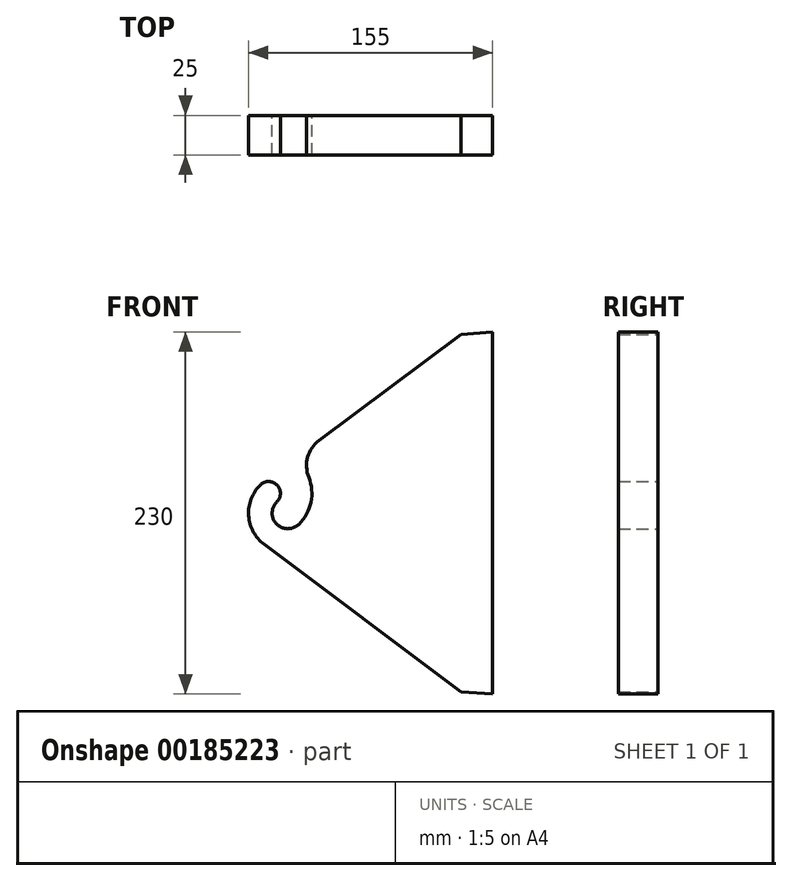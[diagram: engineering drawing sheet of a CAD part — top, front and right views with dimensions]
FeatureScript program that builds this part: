
annotation { "Feature Type Name" : "Feature", "Feature Type Description" : "" }
export const myFeature = defineFeature(function(context is Context, id is Id, definition is map)
    precondition{}
    {
        {
            var Q0;
            Q0=qCreatedBy(makeId("Front.planeOp"),FACE);
            var sketch = newSketch(context, id + "F0", { "sketchPlane" : qUnion([Q0])});
            skCircle(sketch, "E0", {"center": v(-130, 130) * mm, "radius": 105 * mm, "construction": true});
            skCircle(sketch, "E1", {"center": v(-130, 130) * mm, "radius": 26.5 * mm, "construction": true});
            skArc(sketch, "E2", {"start": v(-137, 137.14) * mm, "mid": v(-137.14, 123) * mm, "end": v(-123, 122.86) * mm});
            skLineSegment(sketch, "E3", {"start": v(-130, 130) * mm, "end": v(0, 130) * mm, "construction": true});
            skLineSegment(sketch, "E4", {"start": v(0, 245) * mm, "end": v(0, 15) * mm});
            skArc(sketch, "E5", {"start": v(-147.5, 147.86) * mm, "mid": v(-154.94, 128.34) * mm, "end": v(-144.97, 109.98) * mm});
            skLineSegment(sketch, "E6", {"start": v(0, 245) * mm, "end": v(-19.94, 243.51) * mm});
            skLineSegment(sketch, "E7", {"start": v(-19.94, 243.51) * mm, "end": v(-110.1, 176.1) * mm});
            skLineSegment(sketch, "E8.MirrorCS", {"start": v(-19.94, 16.49) * mm, "end": v(-144.97, 109.98) * mm});
            skLineSegment(sketch, "E9.MirrorCS", {"start": v(0, 15) * mm, "end": v(-19.94, 16.49) * mm});
            skArc(sketch, "E10", {"start": v(-137, 137.14) * mm, "mid": v(-136.9, 147.75) * mm, "end": v(-147.5, 147.86) * mm});
            skArc(sketch, "E11", {"start": v(-153.26, 117.3) * mm, "mid": v(-152.14, 116.84) * mm, "end": v(-151, 116.43) * mm});
            skPoint(sketch, "E12.orphan", {"position": v(-144.97, 150.02) * mm});
            skArc(sketch, "E13.trimOffspring", {"start": v(-123, 122.86) * mm, "mid": v(-115.34, 136.81) * mm, "end": v(-116.7, 152.68) * mm});
            skPoint(sketch, "E14.visualSharp", {"position": v(-125.68, 164.45) * mm});
            skArc(sketch, "E14.filletArc", {"start": v(-110.1, 176.1) * mm, "mid": v(-117.37, 165.5) * mm, "end": v(-116.7, 152.68) * mm});
            skSolve(sketch);
        }
        {
            var Q0;
            Q0=makeQuery(id+"F0.imprint","IMPRINT",FACE,{"disambiguationData":[TD([[makeQuery(id+"F0.imprint","IMPRINT",EDGE,{"derivedFrom":sQuery(id+"F0.wireOp",EDGE,"E2")}),-1.0]])]});
            extrude(context, id + "F1", {"entities" : qUnion([Q0]), "depth" : 25 * mm});
        }
    });
